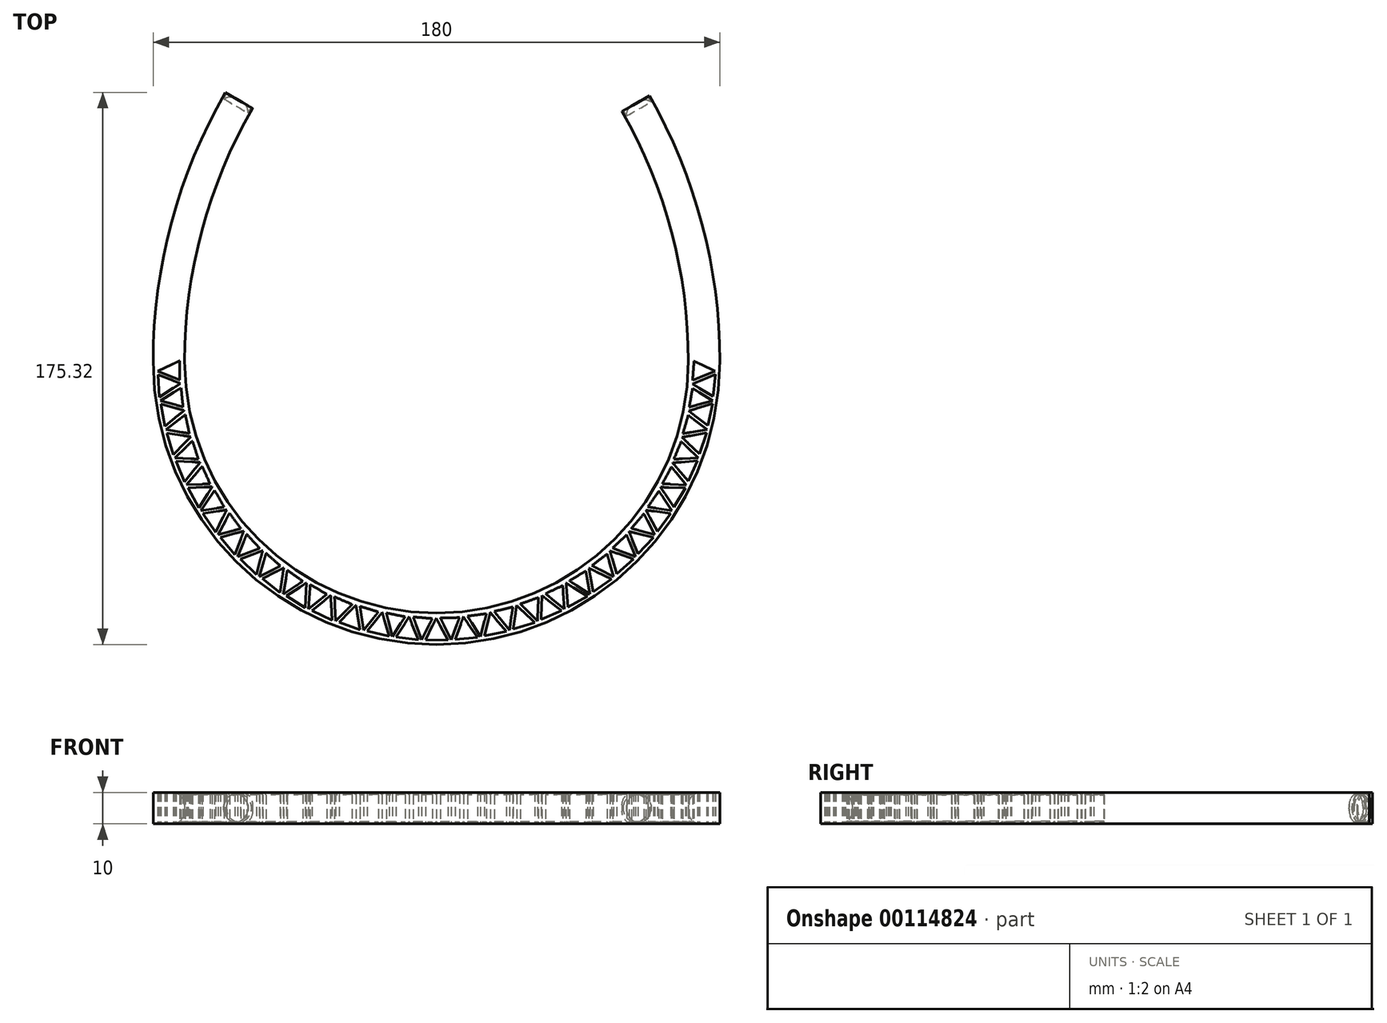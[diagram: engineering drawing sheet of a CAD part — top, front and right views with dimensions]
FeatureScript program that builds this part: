
annotation { "Feature Type Name" : "Feature", "Feature Type Description" : "" }
export const myFeature = defineFeature(function(context is Context, id is Id, definition is map)
    precondition{}
    {
        {
            var Q0;
            Q0=qCreatedBy(makeId("Top.planeOp"),FACE);
            var sketch = newSketch(context, id + "F0", { "sketchPlane" : qUnion([Q0])});
            skArc(sketch, "E0", {"start": v(80, 0) * mm, "mid": v(0, -80) * mm, "end": v(-80, 0) * mm});
            skArc(sketch, "E1", {"start": v(80, 0) * mm, "mid": v(74.65, 41.04) * mm, "end": v(58.94, 79.34) * mm});
            skArc(sketch, "E2", {"start": v(-80, 0) * mm, "mid": v(-74.5, 41.58) * mm, "end": v(-58.4, 80.3) * mm});
            skArc(sketch, "E3.0", {"start": v(-90, 0) * mm, "mid": v(-84.16, 44.18) * mm, "end": v(-67.04, 85.32) * mm});
            skArc(sketch, "E3.1", {"start": v(90, 0) * mm, "mid": v(0, -90) * mm, "end": v(-90, 0) * mm});
            skArc(sketch, "E3.2", {"start": v(90, 0) * mm, "mid": v(84.31, 43.6) * mm, "end": v(67.63, 84.3) * mm});
            skLineSegment(sketch, "E4", {"start": v(-67.04, 85.32) * mm, "end": v(-58.4, 80.3) * mm});
            skLineSegment(sketch, "E5", {"start": v(58.94, 79.34) * mm, "end": v(67.63, 84.3) * mm});
            skLineSegment(sketch, "E6", {"start": v(-99.18, 85.32) * mm, "end": v(-99.18, -90) * mm});
            skPoint(sketch, "E6.endSnap0", {"position": v(0, -90) * mm});
            skSolve(sketch);
        }
        {
            var Q0;
            Q0=qCreatedBy(makeId("Top.planeOp"),FACE);
            var sketch = newSketch(context, id + "F1", { "sketchPlane" : qUnion([Q0])});
            skLineSegment(sketch, "E7", {"start": v(81.8, 0) * mm, "end": v(88.54, -3.24) * mm});
            skLineSegment(sketch, "E8", {"start": v(88.54, -3.24) * mm, "end": v(81.35, -6.07) * mm});
            skLineSegment(sketch, "E9", {"start": v(81.35, -6.07) * mm, "end": v(81.8, 0) * mm});
            skLineSegment(sketch, "E10.1.0", {"start": v(81.34, -8.64) * mm, "end": v(87.7, -12.58) * mm});
            skLineSegment(sketch, "E10.1.1", {"start": v(80.25, -14.63) * mm, "end": v(81.34, -8.64) * mm});
            skLineSegment(sketch, "E10.1.2", {"start": v(87.7, -12.58) * mm, "end": v(80.25, -14.63) * mm});
            skLineSegment(sketch, "E10.2.0", {"start": v(79.97, -17.18) * mm, "end": v(85.88, -21.77) * mm});
            skLineSegment(sketch, "E10.2.1", {"start": v(78.26, -23.02) * mm, "end": v(79.97, -17.18) * mm});
            skLineSegment(sketch, "E10.2.2", {"start": v(85.88, -21.77) * mm, "end": v(78.26, -23.02) * mm});
            skLineSegment(sketch, "E10.3.0", {"start": v(77.71, -25.53) * mm, "end": v(83.1, -30.72) * mm});
            skLineSegment(sketch, "E10.3.1", {"start": v(75.4, -31.16) * mm, "end": v(77.71, -25.53) * mm});
            skLineSegment(sketch, "E10.3.2", {"start": v(83.1, -30.72) * mm, "end": v(75.4, -31.16) * mm});
            skLineSegment(sketch, "E10.4.0", {"start": v(74.58, -33.6) * mm, "end": v(79.4, -39.32) * mm});
            skLineSegment(sketch, "E10.4.1", {"start": v(71.68, -38.95) * mm, "end": v(74.58, -33.6) * mm});
            skLineSegment(sketch, "E10.4.2", {"start": v(79.4, -39.32) * mm, "end": v(71.68, -38.95) * mm});
            skLineSegment(sketch, "E10.5.0", {"start": v(70.61, -41.28) * mm, "end": v(74.8, -47.49) * mm});
            skLineSegment(sketch, "E10.5.1", {"start": v(67.16, -46.3) * mm, "end": v(70.61, -41.28) * mm});
            skLineSegment(sketch, "E10.5.2", {"start": v(74.8, -47.49) * mm, "end": v(67.16, -46.3) * mm});
            skLineSegment(sketch, "E10.6.0", {"start": v(65.86, -48.51) * mm, "end": v(69.37, -55.12) * mm});
            skLineSegment(sketch, "E10.6.1", {"start": v(61.9, -53.13) * mm, "end": v(65.86, -48.51) * mm});
            skLineSegment(sketch, "E10.6.2", {"start": v(69.37, -55.12) * mm, "end": v(61.9, -53.13) * mm});
            skLineSegment(sketch, "E10.7.0", {"start": v(60.37, -55.2) * mm, "end": v(63.16, -62.14) * mm});
            skLineSegment(sketch, "E10.7.1", {"start": v(55.94, -59.37) * mm, "end": v(60.37, -55.2) * mm});
            skLineSegment(sketch, "E10.7.2", {"start": v(63.16, -62.14) * mm, "end": v(55.94, -59.37) * mm});
            skLineSegment(sketch, "E10.8.0", {"start": v(54.2, -61.26) * mm, "end": v(56.24, -68.46) * mm});
            skLineSegment(sketch, "E10.8.1", {"start": v(49.36, -64.95) * mm, "end": v(54.2, -61.26) * mm});
            skLineSegment(sketch, "E10.8.2", {"start": v(56.24, -68.46) * mm, "end": v(49.36, -64.95) * mm});
            skLineSegment(sketch, "E10.9.0", {"start": v(47.43, -66.64) * mm, "end": v(48.7, -74.02) * mm});
            skLineSegment(sketch, "E10.9.1", {"start": v(42.22, -69.8) * mm, "end": v(47.43, -66.64) * mm});
            skLineSegment(sketch, "E10.9.2", {"start": v(48.7, -74.02) * mm, "end": v(42.22, -69.8) * mm});
            skLineSegment(sketch, "E10.10.0", {"start": v(40.12, -71.28) * mm, "end": v(40.6, -78.75) * mm});
            skLineSegment(sketch, "E10.10.1", {"start": v(34.61, -73.87) * mm, "end": v(40.12, -71.28) * mm});
            skLineSegment(sketch, "E10.10.2", {"start": v(40.6, -78.75) * mm, "end": v(34.61, -73.87) * mm});
            skLineSegment(sketch, "E10.11.0", {"start": v(32.37, -75.12) * mm, "end": v(32.06, -82.6) * mm});
            skLineSegment(sketch, "E10.11.1", {"start": v(26.62, -77.11) * mm, "end": v(32.37, -75.12) * mm});
            skLineSegment(sketch, "E10.11.2", {"start": v(32.06, -82.6) * mm, "end": v(26.62, -77.11) * mm});
            skLineSegment(sketch, "E10.12.0", {"start": v(24.26, -78.12) * mm, "end": v(23.16, -85.52) * mm});
            skLineSegment(sketch, "E10.12.1", {"start": v(18.33, -79.5) * mm, "end": v(24.26, -78.12) * mm});
            skLineSegment(sketch, "E10.12.2", {"start": v(23.16, -85.52) * mm, "end": v(18.33, -79.5) * mm});
            skLineSegment(sketch, "E10.13.0", {"start": v(15.87, -80.24) * mm, "end": v(14, -87.49) * mm});
            skLineSegment(sketch, "E10.13.1", {"start": v(9.83, -80.98) * mm, "end": v(15.87, -80.24) * mm});
            skLineSegment(sketch, "E10.13.2", {"start": v(14, -87.49) * mm, "end": v(9.83, -80.98) * mm});
            skLineSegment(sketch, "E10.14.0", {"start": v(7.3, -81.47) * mm, "end": v(4.68, -88.48) * mm});
            skLineSegment(sketch, "E10.14.1", {"start": v(1.22, -81.57) * mm, "end": v(7.3, -81.47) * mm});
            skLineSegment(sketch, "E10.14.2", {"start": v(4.68, -88.48) * mm, "end": v(1.22, -81.57) * mm});
            skLineSegment(sketch, "E10.15.0", {"start": v(-1.34, -81.79) * mm, "end": v(-4.7, -88.48) * mm});
            skLineSegment(sketch, "E10.15.1", {"start": v(-7.4, -81.24) * mm, "end": v(-1.34, -81.79) * mm});
            skLineSegment(sketch, "E10.15.2", {"start": v(-4.7, -88.48) * mm, "end": v(-7.4, -81.24) * mm});
            skLineSegment(sketch, "E10.16.0", {"start": v(-9.97, -81.19) * mm, "end": v(-14, -87.49) * mm});
            skLineSegment(sketch, "E10.16.1", {"start": v(-15.94, -80) * mm, "end": v(-9.97, -81.19) * mm});
            skLineSegment(sketch, "E10.16.2", {"start": v(-14, -87.49) * mm, "end": v(-15.94, -80) * mm});
            skLineSegment(sketch, "E10.17.0", {"start": v(-18.49, -79.68) * mm, "end": v(-23.17, -85.52) * mm});
            skLineSegment(sketch, "E10.17.1", {"start": v(-24.3, -77.87) * mm, "end": v(-18.49, -79.68) * mm});
            skLineSegment(sketch, "E10.17.2", {"start": v(-23.17, -85.52) * mm, "end": v(-24.3, -77.87) * mm});
            skLineSegment(sketch, "E10.18.0", {"start": v(-26.8, -77.28) * mm, "end": v(-32.07, -82.6) * mm});
            skLineSegment(sketch, "E10.18.1", {"start": v(-32.39, -74.87) * mm, "end": v(-26.8, -77.28) * mm});
            skLineSegment(sketch, "E10.18.2", {"start": v(-32.07, -82.6) * mm, "end": v(-32.39, -74.87) * mm});
            skLineSegment(sketch, "E10.19.0", {"start": v(-34.81, -74.02) * mm, "end": v(-40.62, -78.74) * mm});
            skLineSegment(sketch, "E10.19.1", {"start": v(-40.11, -71.03) * mm, "end": v(-34.81, -74.02) * mm});
            skLineSegment(sketch, "E10.19.2", {"start": v(-40.62, -78.74) * mm, "end": v(-40.11, -71.03) * mm});
            skLineSegment(sketch, "E10.20.0", {"start": v(-42.43, -69.93) * mm, "end": v(-48.7, -74.01) * mm});
            skLineSegment(sketch, "E10.20.1", {"start": v(-47.4, -66.4) * mm, "end": v(-42.43, -69.93) * mm});
            skLineSegment(sketch, "E10.20.2", {"start": v(-48.7, -74.01) * mm, "end": v(-47.4, -66.4) * mm});
            skLineSegment(sketch, "E10.21.0", {"start": v(-49.58, -65.06) * mm, "end": v(-56.25, -68.45) * mm});
            skLineSegment(sketch, "E10.21.1", {"start": v(-54.14, -61.02) * mm, "end": v(-49.58, -65.06) * mm});
            skLineSegment(sketch, "E10.21.2", {"start": v(-56.25, -68.45) * mm, "end": v(-54.14, -61.02) * mm});
            skLineSegment(sketch, "E10.22.0", {"start": v(-56.17, -59.46) * mm, "end": v(-63.16, -62.13) * mm});
            skLineSegment(sketch, "E10.22.1", {"start": v(-60.28, -54.96) * mm, "end": v(-56.17, -59.46) * mm});
            skLineSegment(sketch, "E10.22.2", {"start": v(-63.16, -62.13) * mm, "end": v(-60.28, -54.96) * mm});
            skLineSegment(sketch, "E10.23.0", {"start": v(-62.14, -53.2) * mm, "end": v(-69.37, -55.11) * mm});
            skLineSegment(sketch, "E10.23.1", {"start": v(-65.75, -48.29) * mm, "end": v(-62.14, -53.2) * mm});
            skLineSegment(sketch, "E10.23.2", {"start": v(-69.37, -55.11) * mm, "end": v(-65.75, -48.29) * mm});
            skLineSegment(sketch, "E10.24.0", {"start": v(-67.41, -46.33) * mm, "end": v(-74.8, -47.48) * mm});
            skLineSegment(sketch, "E10.24.1", {"start": v(-70.48, -41.08) * mm, "end": v(-67.41, -46.33) * mm});
            skLineSegment(sketch, "E10.24.2", {"start": v(-74.8, -47.48) * mm, "end": v(-70.48, -41.08) * mm});
            skLineSegment(sketch, "E10.25.0", {"start": v(-71.93, -38.95) * mm, "end": v(-79.4, -39.31) * mm});
            skLineSegment(sketch, "E10.25.1", {"start": v(-74.42, -33.4) * mm, "end": v(-71.93, -38.95) * mm});
            skLineSegment(sketch, "E10.25.2", {"start": v(-79.4, -39.31) * mm, "end": v(-74.42, -33.4) * mm});
            skLineSegment(sketch, "E10.26.0", {"start": v(-75.64, -31.14) * mm, "end": v(-83.1, -30.7) * mm});
            skLineSegment(sketch, "E10.26.1", {"start": v(-77.54, -25.36) * mm, "end": v(-75.64, -31.14) * mm});
            skLineSegment(sketch, "E10.26.2", {"start": v(-83.1, -30.7) * mm, "end": v(-77.54, -25.36) * mm});
            skLineSegment(sketch, "E10.27.0", {"start": v(-78.5, -22.98) * mm, "end": v(-85.89, -21.76) * mm});
            skLineSegment(sketch, "E10.27.1", {"start": v(-79.78, -17.02) * mm, "end": v(-78.5, -22.98) * mm});
            skLineSegment(sketch, "E10.27.2", {"start": v(-85.89, -21.76) * mm, "end": v(-79.78, -17.02) * mm});
            skLineSegment(sketch, "E10.28.0", {"start": v(-80.5, -14.56) * mm, "end": v(-87.7, -12.56) * mm});
            skLineSegment(sketch, "E10.28.1", {"start": v(-81.13, -8.5) * mm, "end": v(-80.5, -14.56) * mm});
            skLineSegment(sketch, "E10.28.2", {"start": v(-87.7, -12.56) * mm, "end": v(-81.13, -8.5) * mm});
            skLineSegment(sketch, "E10.29.0", {"start": v(-81.58, -5.97) * mm, "end": v(-88.54, -3.23) * mm});
            skLineSegment(sketch, "E10.29.1", {"start": v(-81.58, 0.11) * mm, "end": v(-81.58, -5.97) * mm});
            skLineSegment(sketch, "E10.29.2", {"start": v(-88.54, -3.23) * mm, "end": v(-81.58, 0.11) * mm});
            skPoint(sketch, "E10.center", {"position": v(0, 0) * mm});
            skLineSegment(sketch, "E10.anchor1", {"start": v(0, 0) * mm, "end": v(81.35, -6.07) * mm, "construction": true});
            skLineSegment(sketch, "E10.anchor2", {"start": v(0, 0) * mm, "end": v(-81.58, 0.11) * mm, "construction": true});
            skLineSegment(sketch, "E11", {"start": v(81.34, -7.26) * mm, "end": v(88.64, -4.16) * mm});
            skLineSegment(sketch, "E12", {"start": v(88.64, -4.16) * mm, "end": v(87.85, -11.25) * mm});
            skLineSegment(sketch, "E13", {"start": v(87.85, -11.25) * mm, "end": v(81.34, -7.26) * mm});
            skLineSegment(sketch, "E14.1.0", {"start": v(87.7, -13.51) * mm, "end": v(86.17, -20.47) * mm});
            skLineSegment(sketch, "E14.1.1", {"start": v(80.12, -15.82) * mm, "end": v(87.7, -13.51) * mm});
            skLineSegment(sketch, "E14.1.2", {"start": v(86.17, -20.47) * mm, "end": v(80.12, -15.82) * mm});
            skLineSegment(sketch, "E14.2.0", {"start": v(85.78, -22.7) * mm, "end": v(83.52, -29.46) * mm});
            skLineSegment(sketch, "E14.2.1", {"start": v(78, -24.2) * mm, "end": v(85.78, -22.7) * mm});
            skLineSegment(sketch, "E14.2.2", {"start": v(83.52, -29.46) * mm, "end": v(78, -24.2) * mm});
            skLineSegment(sketch, "E14.3.0", {"start": v(82.9, -31.65) * mm, "end": v(79.94, -38.13) * mm});
            skLineSegment(sketch, "E14.3.1", {"start": v(75, -32.3) * mm, "end": v(82.9, -31.65) * mm});
            skLineSegment(sketch, "E14.3.2", {"start": v(79.94, -38.13) * mm, "end": v(75, -32.3) * mm});
            skLineSegment(sketch, "E14.4.0", {"start": v(79.1, -40.23) * mm, "end": v(75.46, -46.36) * mm});
            skLineSegment(sketch, "E14.4.1", {"start": v(71.16, -40.06) * mm, "end": v(79.1, -40.23) * mm});
            skLineSegment(sketch, "E14.4.2", {"start": v(75.46, -46.36) * mm, "end": v(71.16, -40.06) * mm});
            skLineSegment(sketch, "E14.5.0", {"start": v(74.4, -48.37) * mm, "end": v(70.13, -54.08) * mm});
            skLineSegment(sketch, "E14.5.1", {"start": v(66.53, -47.35) * mm, "end": v(74.4, -48.37) * mm});
            skLineSegment(sketch, "E14.5.2", {"start": v(70.13, -54.08) * mm, "end": v(66.53, -47.35) * mm});
            skLineSegment(sketch, "E14.6.0", {"start": v(68.87, -55.96) * mm, "end": v(64.02, -61.2) * mm});
            skLineSegment(sketch, "E14.6.1", {"start": v(61.15, -54.12) * mm, "end": v(68.87, -55.96) * mm});
            skLineSegment(sketch, "E14.6.2", {"start": v(64.02, -61.2) * mm, "end": v(61.15, -54.12) * mm});
            skLineSegment(sketch, "E14.7.0", {"start": v(62.57, -62.93) * mm, "end": v(57.2, -67.62) * mm});
            skLineSegment(sketch, "E14.7.1", {"start": v(55.09, -60.28) * mm, "end": v(62.57, -62.93) * mm});
            skLineSegment(sketch, "E14.7.2", {"start": v(57.2, -67.62) * mm, "end": v(55.09, -60.28) * mm});
            skLineSegment(sketch, "E14.8.0", {"start": v(55.56, -69.19) * mm, "end": v(49.73, -73.28) * mm});
            skLineSegment(sketch, "E14.8.1", {"start": v(48.4, -65.77) * mm, "end": v(55.56, -69.19) * mm});
            skLineSegment(sketch, "E14.8.2", {"start": v(49.73, -73.28) * mm, "end": v(48.4, -65.77) * mm});
            skLineSegment(sketch, "E14.9.0", {"start": v(47.94, -74.68) * mm, "end": v(41.7, -78.13) * mm});
            skLineSegment(sketch, "E14.9.1", {"start": v(41.18, -70.52) * mm, "end": v(47.94, -74.68) * mm});
            skLineSegment(sketch, "E14.9.2", {"start": v(41.7, -78.13) * mm, "end": v(41.18, -70.52) * mm});
            skLineSegment(sketch, "E14.10.0", {"start": v(39.78, -79.32) * mm, "end": v(33.21, -82.1) * mm});
            skLineSegment(sketch, "E14.10.1", {"start": v(33.5, -74.48) * mm, "end": v(39.78, -79.32) * mm});
            skLineSegment(sketch, "E14.10.2", {"start": v(33.21, -82.1) * mm, "end": v(33.5, -74.48) * mm});
            skLineSegment(sketch, "E14.11.0", {"start": v(31.17, -83.08) * mm, "end": v(24.35, -85.15) * mm});
            skLineSegment(sketch, "E14.11.1", {"start": v(25.44, -77.6) * mm, "end": v(31.17, -83.08) * mm});
            skLineSegment(sketch, "E14.11.2", {"start": v(24.35, -85.15) * mm, "end": v(25.44, -77.6) * mm});
            skLineSegment(sketch, "E14.12.0", {"start": v(22.21, -85.91) * mm, "end": v(15.2, -87.25) * mm});
            skLineSegment(sketch, "E14.12.1", {"start": v(17.1, -79.85) * mm, "end": v(22.21, -85.91) * mm});
            skLineSegment(sketch, "E14.12.2", {"start": v(15.2, -87.25) * mm, "end": v(17.1, -79.85) * mm});
            skLineSegment(sketch, "E14.13.0", {"start": v(13, -87.78) * mm, "end": v(5.9, -88.37) * mm});
            skLineSegment(sketch, "E14.13.1", {"start": v(8.56, -81.21) * mm, "end": v(13, -87.78) * mm});
            skLineSegment(sketch, "E14.13.2", {"start": v(5.9, -88.37) * mm, "end": v(8.56, -81.21) * mm});
            skLineSegment(sketch, "E14.14.0", {"start": v(3.65, -88.66) * mm, "end": v(-3.47, -88.5) * mm});
            skLineSegment(sketch, "E14.14.1", {"start": v(-0.08, -81.66) * mm, "end": v(3.65, -88.66) * mm});
            skLineSegment(sketch, "E14.14.2", {"start": v(-3.47, -88.5) * mm, "end": v(-0.08, -81.66) * mm});
            skLineSegment(sketch, "E14.15.0", {"start": v(-5.74, -88.55) * mm, "end": v(-12.8, -87.63) * mm});
            skLineSegment(sketch, "E14.15.1", {"start": v(-8.7, -81.2) * mm, "end": v(-5.74, -88.55) * mm});
            skLineSegment(sketch, "E14.15.2", {"start": v(-12.8, -87.63) * mm, "end": v(-8.7, -81.2) * mm});
            skLineSegment(sketch, "E14.16.0", {"start": v(-15.07, -87.45) * mm, "end": v(-22, -85.79) * mm});
            skLineSegment(sketch, "E14.16.1", {"start": v(-17.24, -79.82) * mm, "end": v(-15.07, -87.45) * mm});
            skLineSegment(sketch, "E14.16.2", {"start": v(-22, -85.79) * mm, "end": v(-17.24, -79.82) * mm});
            skLineSegment(sketch, "E14.17.0", {"start": v(-24.23, -85.37) * mm, "end": v(-30.94, -82.98) * mm});
            skLineSegment(sketch, "E14.17.1", {"start": v(-25.58, -77.55) * mm, "end": v(-24.23, -85.37) * mm});
            skLineSegment(sketch, "E14.17.2", {"start": v(-30.94, -82.98) * mm, "end": v(-25.58, -77.55) * mm});
            skLineSegment(sketch, "E14.18.0", {"start": v(-33.12, -82.33) * mm, "end": v(-39.54, -79.25) * mm});
            skLineSegment(sketch, "E14.18.1", {"start": v(-33.64, -74.41) * mm, "end": v(-33.12, -82.33) * mm});
            skLineSegment(sketch, "E14.18.2", {"start": v(-39.54, -79.25) * mm, "end": v(-33.64, -74.41) * mm});
            skLineSegment(sketch, "E14.19.0", {"start": v(-41.63, -78.37) * mm, "end": v(-47.7, -74.62) * mm});
            skLineSegment(sketch, "E14.19.1", {"start": v(-41.32, -70.44) * mm, "end": v(-41.63, -78.37) * mm});
            skLineSegment(sketch, "E14.19.2", {"start": v(-47.7, -74.62) * mm, "end": v(-41.32, -70.44) * mm});
            skLineSegment(sketch, "E14.20.0", {"start": v(-49.68, -73.53) * mm, "end": v(-55.32, -69.16) * mm});
            skLineSegment(sketch, "E14.20.1", {"start": v(-48.53, -65.68) * mm, "end": v(-49.68, -73.53) * mm});
            skLineSegment(sketch, "E14.20.2", {"start": v(-55.32, -69.16) * mm, "end": v(-48.53, -65.68) * mm});
            skLineSegment(sketch, "E14.21.0", {"start": v(-57.18, -67.86) * mm, "end": v(-62.32, -62.93) * mm});
            skLineSegment(sketch, "E14.21.1", {"start": v(-55.2, -60.18) * mm, "end": v(-57.18, -67.86) * mm});
            skLineSegment(sketch, "E14.21.2", {"start": v(-62.32, -62.93) * mm, "end": v(-55.2, -60.18) * mm});
            skLineSegment(sketch, "E14.22.0", {"start": v(-64.03, -61.44) * mm, "end": v(-68.62, -55.99) * mm});
            skLineSegment(sketch, "E14.22.1", {"start": v(-61.25, -54) * mm, "end": v(-64.03, -61.44) * mm});
            skLineSegment(sketch, "E14.22.2", {"start": v(-68.62, -55.99) * mm, "end": v(-61.25, -54) * mm});
            skLineSegment(sketch, "E14.23.0", {"start": v(-70.17, -54.32) * mm, "end": v(-74.16, -48.42) * mm});
            skLineSegment(sketch, "E14.23.1", {"start": v(-66.62, -47.23) * mm, "end": v(-70.17, -54.32) * mm});
            skLineSegment(sketch, "E14.23.2", {"start": v(-74.16, -48.42) * mm, "end": v(-66.62, -47.23) * mm});
            skLineSegment(sketch, "E14.24.0", {"start": v(-75.52, -46.6) * mm, "end": v(-78.86, -40.3) * mm});
            skLineSegment(sketch, "E14.24.1", {"start": v(-71.24, -39.92) * mm, "end": v(-75.52, -46.6) * mm});
            skLineSegment(sketch, "E14.24.2", {"start": v(-78.86, -40.3) * mm, "end": v(-71.24, -39.92) * mm});
            skLineSegment(sketch, "E14.25.0", {"start": v(-80.02, -38.36) * mm, "end": v(-82.68, -31.75) * mm});
            skLineSegment(sketch, "E14.25.1", {"start": v(-75.06, -32.17) * mm, "end": v(-80.02, -38.36) * mm});
            skLineSegment(sketch, "E14.25.2", {"start": v(-82.68, -31.75) * mm, "end": v(-75.06, -32.17) * mm});
            skLineSegment(sketch, "E14.26.0", {"start": v(-83.63, -29.69) * mm, "end": v(-85.57, -22.83) * mm});
            skLineSegment(sketch, "E14.26.1", {"start": v(-78.04, -24.05) * mm, "end": v(-83.63, -29.69) * mm});
            skLineSegment(sketch, "E14.26.2", {"start": v(-85.57, -22.83) * mm, "end": v(-78.04, -24.05) * mm});
            skLineSegment(sketch, "E14.27.0", {"start": v(-86.3, -20.68) * mm, "end": v(-87.5, -13.65) * mm});
            skLineSegment(sketch, "E14.27.1", {"start": v(-80.15, -15.67) * mm, "end": v(-86.3, -20.68) * mm});
            skLineSegment(sketch, "E14.27.2", {"start": v(-87.5, -13.65) * mm, "end": v(-80.15, -15.67) * mm});
            skLineSegment(sketch, "E14.28.0", {"start": v(-88, -11.44) * mm, "end": v(-88.46, -4.33) * mm});
            skLineSegment(sketch, "E14.28.1", {"start": v(-81.35, -7.11) * mm, "end": v(-88, -11.44) * mm});
            skLineSegment(sketch, "E14.28.2", {"start": v(-88.46, -4.33) * mm, "end": v(-81.35, -7.11) * mm});
            skLineSegment(sketch, "E14.anchor1", {"start": v(0, 0) * mm, "end": v(81.34, -7.26) * mm, "construction": true});
            skLineSegment(sketch, "E14.anchor2", {"start": v(0, 0) * mm, "end": v(-81.35, -7.11) * mm, "construction": true});
            skSolve(sketch);
        }
        {
            var Q0;
            Q0 = qSketchRegion(id + "F0", true);
            extrude(context, id + "F2", {"entities" : qUnion([Q0]), "depth" : 10 * mm});
        }
        {
            var Q0;
            Q0=makeQuery(id+"F2.opExtrude","CAP_EDGE",EDGE,{"disambiguationData":[OSD([sQuery(id+"F0.wireOp",EDGE,"E1")])],"isStart":false});
            var Q1;
            Q1=makeQuery(id+"F2.opExtrude","CAP_EDGE",EDGE,{"disambiguationData":[OSD([sQuery(id+"F0.wireOp",EDGE,"E1")])],"isStart":true});
            fillet(context, id + "F3", {"entities" : qUnion([Q0, Q1]), "radius" : 4 * mm, "tangentPropagation" : true, "allowEdgeOverflow" : false});
        }
        {
            var Q0;
            Q0 = qSketchRegion(id + "F1", true);
            extrude(context, id + "F4", {"entities" : qUnion([Q0]), "operationType" : NewBodyOperationType.REMOVE, "depth" : 25 * mm});
        }
        {
            var Q0;
            Q0=makeQuery(id+"F2.opExtrude","SWEPT_FACE",FACE,{"disambiguationData":[OSD([sQuery(id+"F0.wireOp",EDGE,"E5")])]});
            var sketch = newSketch(context, id + "F5", { "sketchPlane" : qUnion([Q0])});
            skCircle(sketch, "E15", {"center": v(-95.53, 4.98) * mm, "radius": 4.5 * mm});
            skSolve(sketch);
        }
        {
            var Q0;
            Q0=makeQuery(id+"F5.imprint","IMPRINT",FACE,{"disambiguationData":[TD([[makeQuery(id+"F5.imprint","IMPRINT",EDGE,{"derivedFrom":sQuery(id+"F5.wireOp",EDGE,"E15")}),1.0]])]});
            extrude(context, id + "F6", {"entities" : qUnion([Q0]), "operationType" : NewBodyOperationType.REMOVE, "oppositeDirection" : true, "depth" : 2 * mm});
        }
        {
            var Q0;
            Q0=makeQuery(id+"F6.boolean.opBoolean","COPY",FACE,{"derivedFrom":makeQuery(id+"F6.opExtrude","CAP_FACE",FACE,{"disambiguationData":[OSD([sQuery(id+"F5.wireOp",EDGE,"E15")])],"isStart":false})});
            var sketch = newSketch(context, id + "F7", { "sketchPlane" : qUnion([Q0])});
            skCircle(sketch, "E16", {"center": v(-95.53, 4.98) * mm, "radius": 4.5 * mm});
            skSolve(sketch);
        }
        {
            var Q0;
            Q0 = qSketchRegion(id + "F7", true);
            extrude(context, id + "F8", {"entities" : qUnion([Q0]), "depth" : 2.1 * mm});
        }
        {
            var Q0;
            Q0=makeQuery(id+"F8.opExtrude","CAP_FACE",FACE,{"disambiguationData":[OSD([sQuery(id+"F7.wireOp",EDGE,"E16")])],"isStart":false});
            fillet(context, id + "F9", {"entities" : qUnion([Q0]), "radius" : 4 * mm, "tangentPropagation" : true, "rho" : 0.5, "crossSection" : FilletCrossSection.CONIC, "allowEdgeOverflow" : false});
        }
        {
            var Q0;
            Q0=makeQuery(id+"F2.opExtrude","SWEPT_FACE",FACE,{"disambiguationData":[OSD([sQuery(id+"F0.wireOp",EDGE,"E4")])]});
            var sketch = newSketch(context, id + "F10", { "sketchPlane" : qUnion([Q0])});
            skCircle(sketch, "E17", {"center": v(95.8, 5) * mm, "radius": 4.5 * mm});
            skSolve(sketch);
        }
        {
            var Q0;
            Q0 = qSketchRegion(id + "F10", true);
            extrude(context, id + "F11", {"entities" : qUnion([Q0]), "operationType" : NewBodyOperationType.REMOVE, "oppositeDirection" : true, "depth" : 2 * mm});
        }
        {
            var Q0;
            Q0=makeQuery(id+"F11.boolean.opBoolean","COPY",FACE,{"derivedFrom":makeQuery(id+"F11.opExtrude","CAP_FACE",FACE,{"disambiguationData":[OSD([sQuery(id+"F10.wireOp",EDGE,"E17")])],"isStart":false})});
            var sketch = newSketch(context, id + "F12", { "sketchPlane" : qUnion([Q0])});
            skCircle(sketch, "E18", {"center": v(95.8, 5) * mm, "radius": 4.45 * mm});
            skSolve(sketch);
        }
        {
            var Q0;
            Q0 = qSketchRegion(id + "F12", true);
            extrude(context, id + "F13", {"entities" : qUnion([Q0]), "operationType" : NewBodyOperationType.ADD, "depth" : 2.1 * mm});
        }
        {
            var Q0;
            Q0=makeQuery(id+"F13.opExtrude","CAP_FACE",FACE,{"disambiguationData":[OSD([sQuery(id+"F12.wireOp",EDGE,"E18")])],"isStart":false});
            fillet(context, id + "F14", {"entities" : qUnion([Q0]), "radius" : 4 * mm, "tangentPropagation" : true, "rho" : 0.5, "crossSection" : FilletCrossSection.CONIC, "allowEdgeOverflow" : false});
        }
    });
